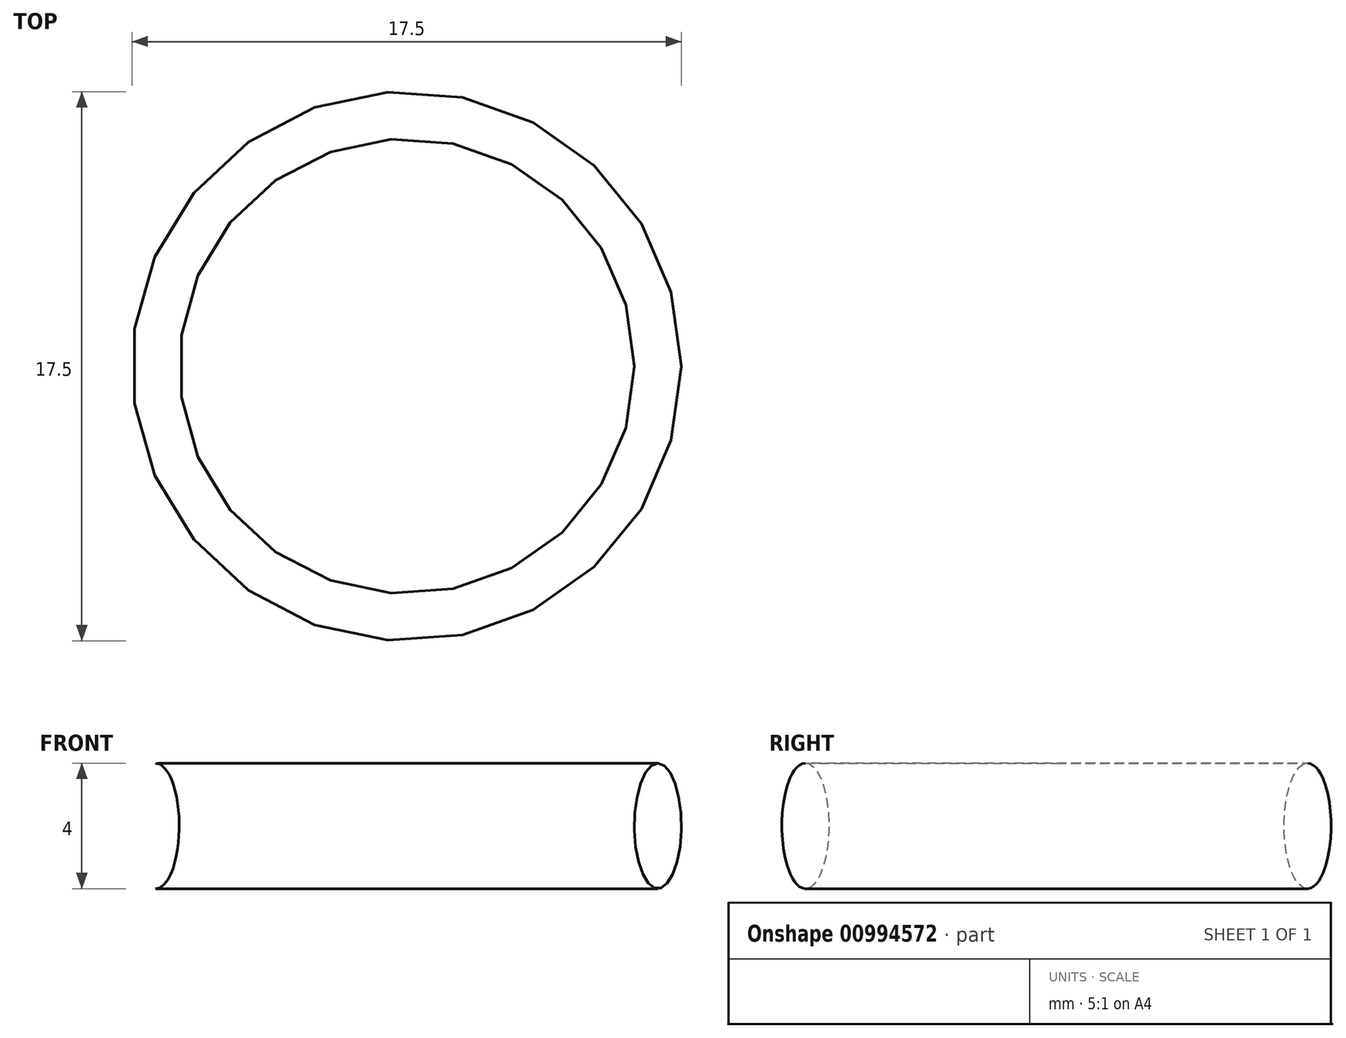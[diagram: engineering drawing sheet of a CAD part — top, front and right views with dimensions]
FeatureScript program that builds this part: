
annotation { "Feature Type Name" : "Feature", "Feature Type Description" : "" }
export const myFeature = defineFeature(function(context is Context, id is Id, definition is map)
    precondition{}
    {
        {
            var Q0;
            Q0=qCreatedBy(makeId("Front.planeOp"),FACE);
            var sketch = newSketch(context, id + "F0", { "sketchPlane" : qUnion([Q0])});
            skEllipse(sketch, "E0", {"center": v(0, 0) * mm, "majorRadius": 2 * mm, "minorRadius": 0.75 * mm, "majorAxis": v(0, 1)});
            skLineSegment(sketch, "E1", {"start": v(-8, 8.5) * mm, "end": v(-8, -9.16) * mm, "construction": true});
            skSolve(sketch);
        }
        {
            var Q0;
            Q0=makeQuery(id+"F0.imprint","IMPRINT",FACE,{"disambiguationData":[TD([[makeQuery(id+"F0.imprint","IMPRINT",EDGE,{"derivedFrom":sQuery(id+"F0.wireOp",EDGE,"E0")}),1.0]])]});
            var Q1;
            Q1=sQuery(id+"F0.wireOp",EDGE,"E0");
            var Q2;
            Q2=sQuery(id+"F0.wireOp",EDGE,"E1");
            revolve(context, id + "F1", {"surfaceOperationType" : NewSurfaceOperationType.NEW, "entities" : qUnion([Q0]), "surfaceEntities" : qUnion([Q1]), "axis" : qUnion([Q2]), "revolveType" : RevolveType.FULL});
        }
    });
